# Revit family: Condensing-Solar-Storage-Water-Heater-Gas_AO_Smith-SGS_80_N
name_source: partatom
category: Mechanical Equipment
revit_build: Autodesk Revit 2014 (Build: 20140709_2115(x64)
units: mm (PartAtom-declared; Revit-internal decimal feet)

## types (1)
- Condensing-Solar-Storage-Water-Heater-Gas_AO_Smith-SGS_80_N
    (Additional Control) Frequency = 50 Hz
    (Additional Control) Phase = 1
    (Additional Control) Power Consumption (nominal) = 700 W
    (Additional Control) Voltage = 230 V
    1e Maintenance (check-up) = 3 maanden na installatie
    2nd Maintenance (general maintenance) = 12 maanden na installatie
    APS Pressure < = 210.0 Pa
    Assembly Code = D3010
    BIM Content Developer = CAD & Company
    CE-PIN = 0063BU3889
    Co2 Emissions (tol. +/- 1.0) vol% = 8.9/9.3
    Cold Water Connection R = 1 1/2"
    Condens Discharge Connection = 40 mm  [stored 0.131234 ft]
    Default Setpoint = 65 °C
    Description = HR-Condenserende Gas-Zonneboiler i.c.m. IT-voorraadvat
    Destination / Country = Nederland
    Diameter = 850 mm  [stored 2.78871 ft]
    Drain Valve Connection Rp = 3/4"
    Draw-off Capacity @ ΔT = 28°C after 120 min. = 5600.0 L
    Draw-off Capacity @ ΔT = 28°C after 30 min. = 1700.0 L
    Draw-off Capacity @ ΔT = 28°C after 60 min. = 3000.0 L
    Draw-off Capacity @ ΔT = 28°C after 90 min. = 4300.0 L
    Draw-off Capacity @ ΔT = 44°C after 120 min. = 3500.0 L
    Draw-off Capacity @ ΔT = 44°C after 30 min. = 940.0 L
    Draw-off Capacity @ ΔT = 44°C after 60 min. = 1800.0 L
    Draw-off Capacity @ ΔT = 44°C after 90 min. = 2600.0 L
    Draw-off Capacity @ ΔT = 50°C after 120 min. = 3000.0 L
    Draw-off Capacity @ ΔT = 50°C after 30 min. = 780.0 L
    Draw-off Capacity @ ΔT = 50°C after 60 min. = 1600.0 L
    Draw-off Capacity @ ΔT = 50°C after 90 min. = 2300.0 L
    Draw-off Capacity @ ΔT = 55°C after 120 min. = 2700.0 L
    Draw-off Capacity @ ΔT = 55°C after 30 min. = 670.0 L
    Draw-off Capacity @ ΔT = 55°C after 60 min. = 1400.0 L
    Draw-off Capacity @ ΔT = 55°C after 90 min. = 2000.0 L
    Draw-off Capacity @ ΔT = 70°C after 120 min. = 0.0 L
    Draw-off Capacity @ ΔT = 70°C after 30 min. = 0.0 L
    Draw-off Capacity @ ΔT = 70°C after 60 min. = 0.0 L
    Draw-off Capacity @ ΔT = 70°C after 90 min. = 0.0 L
    Empty Weight = 480 kg
    Energy Efficiency Rating (Hi, acc NEN-EN 89-1999) = 108
    Energy Efficiency Rating (Hs, acc NEN-EN 89-1999) = 97
    Flue Diameter - concentric system = 130/200 mm/mm
    Flue Diameter - parallel system = 130 mm  [stored 0.426509 ft]
    Flue Diameter - water heater = 130/200 mm/mm
    Frequency = 50 Hz
    Gas Category = II2EK3B/P
    Gas Connection R = 3/4"
    Gas Flow Rate - Mass kg/h = 0
    Gas Flow Rate - Volume ltr/hr = 8.30/9.70
    Heating Up Time @ ΔT = 28°C = 11
    Heating Up Time @ ΔT = 44°C = 17
    Heating Up Time @ ΔT = 50°C = 20
    Heating Up Time @ ΔT = 55°C = 22
    Heating Up Time @ ΔT = 70°C = 0
    Height = 2060 mm  [stored 6.75853 ft]
    Height Air Inlet = 1995 mm  [stored 6.54528 ft]
    Height Cold water Intlet = 225 mm  [stored 0.738189 ft]
    Height Flue Outlet = 1995 mm  [stored 6.54528 ft]
    Height Gas Connection = 1855 mm  [stored 6.08596 ft]
    Height Warm Water Outlet = 2060 mm  [stored 6.75853 ft]
    Hot / Warm Water Connection R = 1 1/2"
    Installation Type = B23/C13/C33/C43/C53/C63
    Insulation Thickness = 44 mm  [stored 0.144357 ft]
    Length = 1000 mm  [stored 3.28084 ft]
    Maintenance Interval = 12 maanden
    Manufacturer = A.O. Smith Water Products Company b.v.
    Manufacturer Number = E 7110
    Max. Flue Gas Outlet Temperature = 50 °C
    Max. Operating Pressure = 800000.0 Pa
    Max. Setpoint = 80 °C
    Min. Setpoint = 40 °C
    Model = SGS 80 N
    NOx Emissions (air free, 0% O2) ppm = 19
    NOx Emissions mg/kWh = 34
    Noice-level dB (A) = 45
    Nominal Heat Input (Gross) = 86600.0/89100.0
    Nominal Heat Input (Net) = 78000.0/80300.0
    Nominal Output = 84200.0/86700.0
    Operating Weight = 960 kg
    Packaging Height = 2060 mm  [stored 6.75853 ft]
    Packaging Length = 1020 mm  [stored 3.34646 ft]
    Packaging Width = 920 mm  [stored 3.01837 ft]
    Phase = 1
    Power Consumption (nominal) = 95 W
    Product Documentation Link = https://www.aosmithinternational.com
    Product Instruction Link = https://www.aosmithinternational.com
    Recovery Rate @ ΔT = 28°C = 2600.0 L/s
    Recovery Rate @ ΔT = 44°C = 1700.0 L/s
    Recovery Rate @ ΔT = 50°C = 1500.0 L/s
    Recovery Rate @ ΔT = 55°C = 1400.0 L/s
    Recovery Rate @ ΔT = 70°C = 0.0 L/s
    Seasonal Energy Efficiency Rating = 97
    Serial Number = 8717449192235
    Stand-by Loss = 0 W
    Stand-by Loss - daily (24h) = 0 W
    Standard Set For = G25.3
    Storage Capacity = 480.0 L
    Supply Pressure = 2000/2500
    T&P Connection Rp = 1"
    Transport Weight = 491 kg
    Type of Packaging = Plastic Krimpverpakking, Karton en Hout
    URL = www.aosmith.nl
    Voltage = 230 V
    Warranty on parts = 12 maanden
    Warranty on tank = 36 maanden
    Width = 900 mm  [stored 2.95276 ft]

note: [stored X ft] marks values corroborated as IEEE doubles in the binary element streams (Revit-internal decimal feet)

## geometry (parser evidence)
native form markers: Blend x18, Sweep x36
no freeform markers — native parametric forms only
